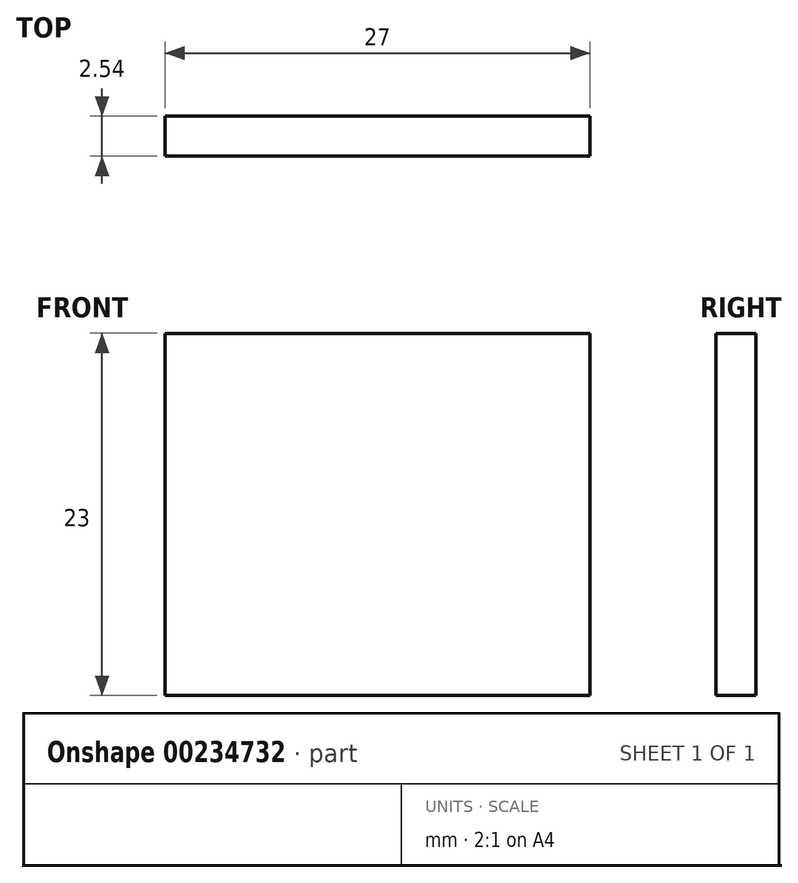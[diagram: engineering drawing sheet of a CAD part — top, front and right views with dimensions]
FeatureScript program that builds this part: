
annotation { "Feature Type Name" : "Feature", "Feature Type Description" : "" }
export const myFeature = defineFeature(function(context is Context, id is Id, definition is map)
    precondition{}
    {
        {
            var Q0;
            Q0=qCreatedBy(makeId("Front.planeOp"),FACE);
            var sketch = newSketch(context, id + "F0", { "sketchPlane" : qUnion([Q0])});
            skLineSegment(sketch, "E0.bottom", {"start": v(-71.35, 19.08) * mm, "end": v(-7.85, 19.08) * mm});
            skLineSegment(sketch, "E0.top", {"start": v(-71.35, -46.96) * mm, "end": v(-7.85, -46.96) * mm});
            skLineSegment(sketch, "E0.left", {"start": v(-71.35, 19.08) * mm, "end": v(-71.35, -46.96) * mm});
            skLineSegment(sketch, "E0.right", {"start": v(-7.85, 19.08) * mm, "end": v(-7.85, -46.96) * mm});
            skLineSegment(sketch, "E1.bottom", {"start": v(-71.35, 19.08) * mm, "end": v(-44.35, 19.08) * mm});
            skLineSegment(sketch, "E1.top", {"start": v(-71.35, -3.92) * mm, "end": v(-44.35, -3.92) * mm});
            skLineSegment(sketch, "E1.left", {"start": v(-71.35, 19.08) * mm, "end": v(-71.35, -3.92) * mm});
            skLineSegment(sketch, "E1.right", {"start": v(-44.35, 19.08) * mm, "end": v(-44.35, -3.92) * mm});
            skEllipse(sketch, "E2", {"center": v(-58.56, -26.94) * mm, "majorRadius": 15.1 * mm, "minorRadius": 9.24 * mm, "majorAxis": v(0, 1)});
            skCircle(sketch, "E3", {"center": v(-10.85, -43.96) * mm, "radius": 1.4 * mm});
            skCircle(sketch, "E4", {"center": v(-68.35, -6.92) * mm, "radius": 1.4 * mm});
            skCircle(sketch, "E5", {"center": v(-10.85, 16.08) * mm, "radius": 1.4 * mm});
            skCircle(sketch, "E6", {"center": v(-68.35, -43.96) * mm, "radius": 1.4 * mm});
            skSolve(sketch);
        }
        {
            var Q0;
            Q0=makeQuery(id+"F0.imprint","IMPRINT",FACE,{"disambiguationData":[TD([[makeQuery(id+"F0.imprint","IMPRINT",EDGE,{"derivedFrom":sQuery(id+"F0.wireOp",EDGE,"E0.bottom")}),-1.0]])]});
            extrude(context, id + "F1", {"entities" : qUnion([Q0]), "depth" : 2.54 * mm});
        }
    });
